# Revit family: Pet_Fountain_Receptor-Pedestal_Mounted-Murdock_Manufacturing-M-PM3X_Series.rfazzz
name_source: partatom
category: Plumbing Fixtures
units: mm (PartAtom-declared; Revit-internal decimal feet)

## family parameters
Cut with Voids When Loaded = No
Host = Face
OmniClass Number = 23.65.70.14.11
OmniClass Title = Drinking Fountains/Coolers
Part Type = Normal
Room Calculation Point = No
Round Connector Dimension = Use Diameter
Shared = Yes

## types (4) — shared parameters
- IAP In-Ground Anchor Plate = No
- LOGO Customer Specified Logo = No
-FRU1 - Underground Freeze-Resistant Valve for One Pushbutton = No
Activation = Push Button
Assembly Code = D2010810
Bowl Diameter = 12"
CW Connection = Yes
CWFU = 1.5
Cold Water Connection Diameter = 1/4"
Compliance Certifications = NSF/ANSI 61, Public Law 111-380 (NO-LEAD)
Default Elevation = 0"
Description = Round Pedestal Push Button Pet Fountain Receptor
Finish- Fountain Bowl = Stainless Steel-Murdock-Polished
HW Connection = No
Height = 32"
Installation Instruction Link = https://www.murdockmfg.com
Installation Type = Pedestal Mounted
Manufacturer = Murdock Manufacturing
Maximum Pressure (PSI) = 30 to 100 PSI
Product Documentation Link = https://www.murdockmfg.com
Product Page URL = https://www.murdockmfg.com
URL = http://www.murdockmfg.com
Vent Connection = No
WFU = 2
Warranty Documentation Link = https://www.murdockmfg.com
Waste Connection = Yes
Waste Connection Diameter = 1 1/4"
Water Pressure = 20-105 psig
cUPC Compliant = Yes
zero-valued in all types: HWFU

## per-type parameters (varying)
| type | Finish | Material |
| M-PM35 | Stainless_Steel-Murdock-12_Gauge-Green_Powder_Coated | Stainless_Steel-Murdock-12_Gauge-Green_Powder_Coated |
| M-PM34 | Stainless_Steel-Murdock-Satin | Stainless_Steel-Murdock-Satin |
| M-PM36 | Stainless_Steel-Murdock-12_Gauge-Red_Powder_Coated | Stainless_Steel-Murdock-12_Gauge-Red_Powder_Coated |
| M-PM37 | Stainless_Steel-Murdock-12_Gauge-Blue_Powder_Coated | Stainless_Steel-Murdock-12_Gauge-Blue_Powder_Coated |

note: column(s) folded — value = type name in every type: Model

## geometry (parser evidence)
native form markers: Sweep x2
no freeform markers — native parametric forms only
